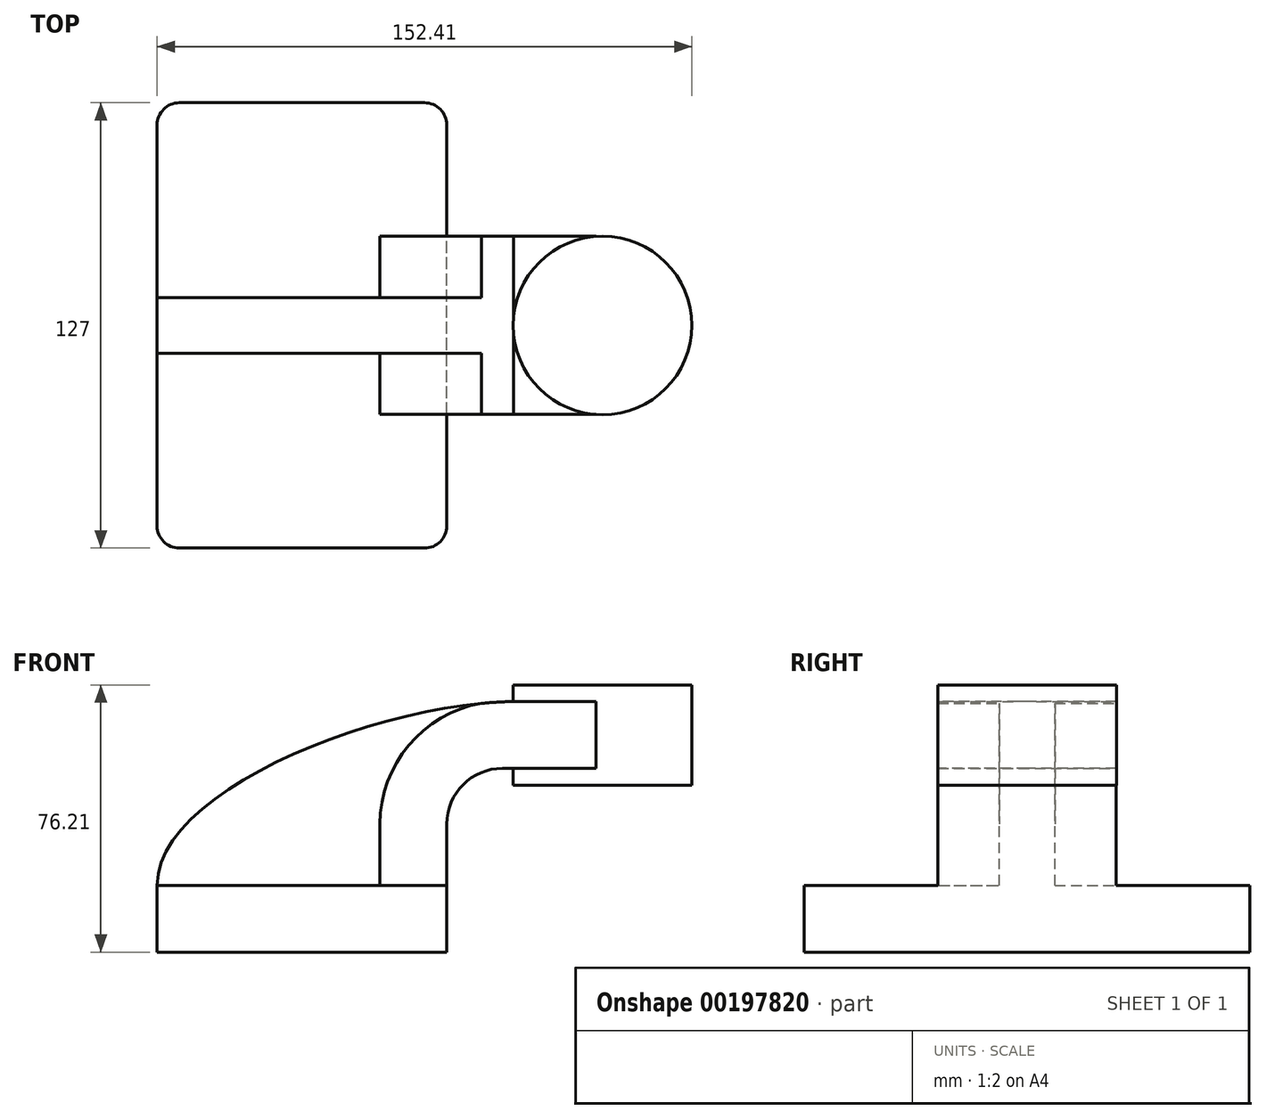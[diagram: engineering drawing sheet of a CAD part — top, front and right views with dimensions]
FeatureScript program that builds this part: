
annotation { "Feature Type Name" : "Feature", "Feature Type Description" : "" }
export const myFeature = defineFeature(function(context is Context, id is Id, definition is map)
    precondition{}
    {
        {
            var Q0;
            Q0=qCreatedBy(makeId("Front.planeOp"),FACE);
            var sketch = newSketch(context, id + "F0", { "sketchPlane" : qUnion([Q0])});
            skLineSegment(sketch, "E0.bottom", {"start": v(-41.27, -9.53) * mm, "end": v(41.28, -9.53) * mm});
            skLineSegment(sketch, "E0.top", {"start": v(-41.28, 9.53) * mm, "end": v(41.28, 9.53) * mm});
            skLineSegment(sketch, "E0.left", {"start": v(-41.28, -9.53) * mm, "end": v(-41.28, 9.53) * mm});
            skLineSegment(sketch, "E0.right", {"start": v(41.28, -9.53) * mm, "end": v(41.28, 9.52) * mm});
            skPoint(sketch, "E0.middle", {"position": v(0, 0) * mm});
            skLineSegment(sketch, "E1.bottom", {"start": v(60.32, 38.1) * mm, "end": v(111.12, 38.1) * mm});
            skLineSegment(sketch, "E1.top", {"start": v(60.32, 66.67) * mm, "end": v(111.12, 66.67) * mm});
            skLineSegment(sketch, "E1.left", {"start": v(60.32, 38.1) * mm, "end": v(60.32, 66.67) * mm});
            skLineSegment(sketch, "E1.right", {"start": v(111.12, 38.1) * mm, "end": v(111.12, 66.67) * mm});
            skPoint(sketch, "E1.middle", {"position": v(85.72, 52.39) * mm});
            skLineSegment(sketch, "E2", {"start": v(41.28, 9.53) * mm, "end": v(41.28, 27) * mm});
            skArc(sketch, "E3", {"start": v(41.28, 27) * mm, "mid": v(45.92, 38.23) * mm, "end": v(57.15, 42.88) * mm});
            skLineSegment(sketch, "E4", {"start": v(57.15, 42.88) * mm, "end": v(85.66, 42.88) * mm});
            skLineSegment(sketch, "E5.0", {"start": v(57.15, 61.93) * mm, "end": v(85.66, 61.93) * mm});
            skArc(sketch, "E5.1", {"start": v(22.23, 27) * mm, "mid": v(32.45, 51.7) * mm, "end": v(57.15, 61.93) * mm});
            skLineSegment(sketch, "E5.2", {"start": v(22.22, 9.53) * mm, "end": v(22.22, 27) * mm});
            skLineSegment(sketch, "E6", {"start": v(85.66, 38.1) * mm, "end": v(85.66, 66.67) * mm});
            skFitSpline(sketch, "E7", {"points": [v(-41.27, 9.53) * mm, v(60.32, 61.93) * mm], "startDerivative": vector(-0.12, 80.8) * mm, "endDerivative": vector(118.14, 1.65) * mm});
            skSolve(sketch);
        }
        {
            var Q0;
            Q0=makeQuery(id+"F0.imprint","IMPRINT",FACE,{"disambiguationData":[TD([[makeQuery(id+"F0.imprint","IMPRINT",EDGE,{"derivedFrom":sQuery(id+"F0.wireOp",EDGE,"E0.bottom")}),1.0]])]});
            extrude(context, id + "F1", {"entities" : qUnion([Q0]), "endBound" : BoundingType.SYMMETRIC, "depth" : 127 * mm});
        }
        {
            var Q0;
            {var subQ1=sQuery(id+"F0.wireOp",EDGE,"E2");Q0=makeQuery(id+"F0.imprint","IMPRINT",FACE,{"disambiguationData":[TD([[makeQuery(id+"F0.imprint","IMPRINT",EDGE,{"derivedFrom":subQ1}),1.0]])]});}
            var Q1;
            {var subQ3=sQuery(id+"F0.wireOp",EDGE,"E4");var subQ5=sQuery(id+"F0.wireOp",EDGE,"E6");var subQ6=makeQuery(id+"F0.imprint","INTERSECT",VERTEX,{"derivedFrom":[subQ3,subQ5]});Q1=makeQuery(id+"F0.imprint","IMPRINT",FACE,{"disambiguationData":[TD([[makeQuery(id+"F0.imprint","IMPRINT",EDGE,{"disambiguationData":[TD([[subQ6,1.0]])],"derivedFrom":subQ3}),1.0]])]});}
            extrude(context, id + "F2", {"entities" : qUnion([Q0, Q1]), "operationType" : NewBodyOperationType.ADD, "endBound" : BoundingType.SYMMETRIC, "depth" : 50.8 * mm});
        }
        {
            var Q0;
            {var subQ3=sQuery(id+"F0.wireOp",EDGE,"E5.2");Q0=makeQuery(id+"F0.imprint","IMPRINT",FACE,{"disambiguationData":[TD([[makeQuery(id+"F0.imprint","IMPRINT",EDGE,{"derivedFrom":subQ3}),1.0]])]});}
            extrude(context, id + "F3", {"entities" : qUnion([Q0]), "operationType" : NewBodyOperationType.ADD, "endBound" : BoundingType.SYMMETRIC, "depth" : 15.88 * mm});
        }
        {
            var Q0;
            {var subQ0=sQuery(id+"F0.wireOp",EDGE,"E1.right");Q0=makeQuery(id+"F0.imprint","IMPRINT",FACE,{"disambiguationData":[TD([[makeQuery(id+"F0.imprint","IMPRINT",EDGE,{"derivedFrom":subQ0}),1.0]])]});}
            var Q1;
            Q1=sQuery(id+"F0.wireOp",EDGE,"E6");
            revolve(context, id + "F4", {"operationType" : NewBodyOperationType.ADD, "entities" : qUnion([Q0]), "axis" : qUnion([Q1]), "revolveType" : RevolveType.FULL});
        }
        {
            var Q0;
            Q0=makeQuery(id+"F1.opExtrude","CAP_EDGE",EDGE,{"disambiguationData":[OSD([sQuery(id+"F0.wireOp",EDGE,"E0.left")])],"isStart":false});
            var Q1;
            Q1=makeQuery(id+"F1.opExtrude","CAP_EDGE",EDGE,{"disambiguationData":[OSD([sQuery(id+"F0.wireOp",EDGE,"E0.right")])],"isStart":false});
            var Q2;
            Q2=makeQuery(id+"F1.opExtrude","CAP_EDGE",EDGE,{"disambiguationData":[OSD([sQuery(id+"F0.wireOp",EDGE,"E0.right")])],"isStart":true});
            var Q3;
            Q3=makeQuery(id+"F1.opExtrude","CAP_EDGE",EDGE,{"disambiguationData":[OSD([sQuery(id+"F0.wireOp",EDGE,"E0.left")])],"isStart":true});
            fillet(context, id + "F5", {"entities" : qUnion([Q0, Q1, Q2, Q3]), "radius" : 6.35 * mm, "tangentPropagation" : true, "allowEdgeOverflow" : false});
        }
    });
